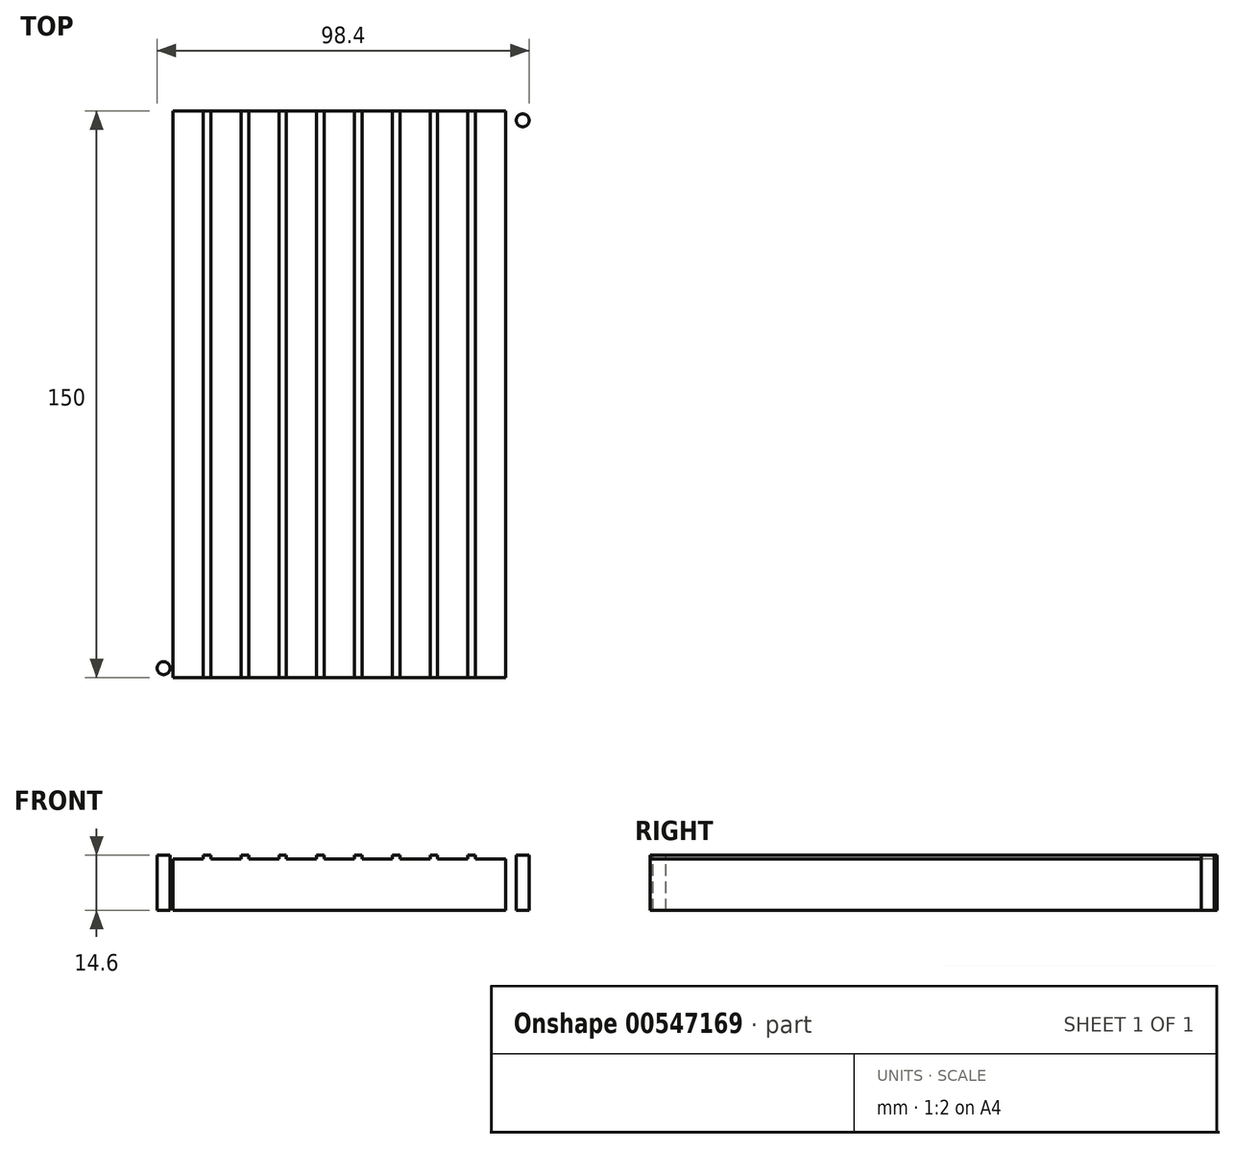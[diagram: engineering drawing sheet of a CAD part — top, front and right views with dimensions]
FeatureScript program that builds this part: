
annotation { "Feature Type Name" : "Feature", "Feature Type Description" : "" }
export const myFeature = defineFeature(function(context is Context, id is Id, definition is map)
    precondition{}
    {
        {
            var Q0;
            Q0=qCreatedBy(makeId("Top.planeOp"),FACE);
            var sketch = newSketch(context, id + "F0", { "sketchPlane" : qUnion([Q0])});
            skLineSegment(sketch, "E0.bottom", {"start": v(0, 0) * mm, "end": v(100, 0) * mm});
            skLineSegment(sketch, "E0.top", {"start": v(0, -150) * mm, "end": v(100, -150) * mm});
            skLineSegment(sketch, "E0.left", {"start": v(0, 0) * mm, "end": v(0, -150) * mm});
            skLineSegment(sketch, "E0.right", {"start": v(100, 0) * mm, "end": v(100, -150) * mm});
            skSolve(sketch);
        }
        {
            var Q0;
            Q0=makeQuery(id+"F0.imprint","IMPRINT",FACE,{"disambiguationData":[TD([[makeQuery(id+"F0.imprint","IMPRINT",EDGE,{"derivedFrom":sQuery(id+"F0.wireOp",EDGE,"E0.bottom")}),-1.0]])]});
            extrude(context, id + "F1", {"entities" : qUnion([Q0]), "depth" : 14.6 * mm, "offsetDistance" : 25 * mm});
        }
        {
            var Q0;
            Q0=makeQuery(id+"F1.opExtrude","CAP_FACE",FACE,{"disambiguationData":[OSD([sQuery(id+"F0.wireOp",EDGE,"E0.bottom"),sQuery(id+"F0.wireOp",EDGE,"E0.top"),sQuery(id+"F0.wireOp",EDGE,"E0.left"),sQuery(id+"F0.wireOp",EDGE,"E0.right")])],"isStart":false});
            var sketch = newSketch(context, id + "F2", { "sketchPlane" : qUnion([Q0])});
            skLineSegment(sketch, "E1.bottom", {"start": v(5, 0) * mm, "end": v(13, 0) * mm});
            skLineSegment(sketch, "E1.top", {"start": v(5, -150) * mm, "end": v(13, -150) * mm});
            skLineSegment(sketch, "E1.left", {"start": v(5, 0) * mm, "end": v(5, -150) * mm});
            skLineSegment(sketch, "E1.right", {"start": v(13, 0) * mm, "end": v(13, -150) * mm});
            skLineSegment(sketch, "E2.1.0.0", {"start": v(15, 0) * mm, "end": v(23, 0) * mm});
            skLineSegment(sketch, "E2.1.0.1", {"start": v(23, 0) * mm, "end": v(23, -150) * mm});
            skLineSegment(sketch, "E2.1.0.2", {"start": v(15, -150) * mm, "end": v(23, -150) * mm});
            skLineSegment(sketch, "E2.1.0.3", {"start": v(15, 0) * mm, "end": v(15, -150) * mm});
            skLineSegment(sketch, "E2.2.0.0", {"start": v(25, 0) * mm, "end": v(33, 0) * mm});
            skLineSegment(sketch, "E2.2.0.1", {"start": v(33, 0) * mm, "end": v(33, -150) * mm});
            skLineSegment(sketch, "E2.2.0.2", {"start": v(25, -150) * mm, "end": v(33, -150) * mm});
            skLineSegment(sketch, "E2.2.0.3", {"start": v(25, 0) * mm, "end": v(25, -150) * mm});
            skLineSegment(sketch, "E2.3.0.0", {"start": v(35, 0) * mm, "end": v(43, 0) * mm});
            skLineSegment(sketch, "E2.3.0.1", {"start": v(43, 0) * mm, "end": v(43, -150) * mm});
            skLineSegment(sketch, "E2.3.0.2", {"start": v(35, -150) * mm, "end": v(43, -150) * mm});
            skLineSegment(sketch, "E2.3.0.3", {"start": v(35, 0) * mm, "end": v(35, -150) * mm});
            skLineSegment(sketch, "E2.4.0.0", {"start": v(45, 0) * mm, "end": v(53, 0) * mm});
            skLineSegment(sketch, "E2.4.0.1", {"start": v(53, 0) * mm, "end": v(53, -150) * mm});
            skLineSegment(sketch, "E2.4.0.2", {"start": v(45, -150) * mm, "end": v(53, -150) * mm});
            skLineSegment(sketch, "E2.4.0.3", {"start": v(45, 0) * mm, "end": v(45, -150) * mm});
            skLineSegment(sketch, "E2.5.0.0", {"start": v(55, 0) * mm, "end": v(63, 0) * mm});
            skLineSegment(sketch, "E2.5.0.1", {"start": v(63, 0) * mm, "end": v(63, -150) * mm});
            skLineSegment(sketch, "E2.5.0.2", {"start": v(55, -150) * mm, "end": v(63, -150) * mm});
            skLineSegment(sketch, "E2.5.0.3", {"start": v(55, 0) * mm, "end": v(55, -150) * mm});
            skLineSegment(sketch, "E2.6.0.0", {"start": v(65, 0) * mm, "end": v(73, 0) * mm});
            skLineSegment(sketch, "E2.6.0.1", {"start": v(73, 0) * mm, "end": v(73, -150) * mm});
            skLineSegment(sketch, "E2.6.0.2", {"start": v(65, -150) * mm, "end": v(73, -150) * mm});
            skLineSegment(sketch, "E2.6.0.3", {"start": v(65, 0) * mm, "end": v(65, -150) * mm});
            skLineSegment(sketch, "E2.7.0.0", {"start": v(75, 0) * mm, "end": v(83, 0) * mm});
            skLineSegment(sketch, "E2.7.0.1", {"start": v(83, 0) * mm, "end": v(83, -150) * mm});
            skLineSegment(sketch, "E2.7.0.2", {"start": v(75, -150) * mm, "end": v(83, -150) * mm});
            skLineSegment(sketch, "E2.7.0.3", {"start": v(75, 0) * mm, "end": v(75, -150) * mm});
            skLineSegment(sketch, "E2.8.0.0", {"start": v(85, 0) * mm, "end": v(93, 0) * mm});
            skLineSegment(sketch, "E2.8.0.1", {"start": v(93, 0) * mm, "end": v(93, -150) * mm});
            skLineSegment(sketch, "E2.8.0.2", {"start": v(85, -150) * mm, "end": v(93, -150) * mm});
            skLineSegment(sketch, "E2.8.0.3", {"start": v(85, 0) * mm, "end": v(85, -150) * mm});
            skLineSegment(sketch, "E2.direction1", {"start": v(5, 0) * mm, "end": v(15, 0) * mm, "construction": true});
            skSolve(sketch);
        }
        {
            var Q0;
            Q0=makeQuery(id+"F2.imprint","IMPRINT",FACE,{"disambiguationData":[TD([[makeQuery(id+"F2.imprint","IMPRINT",EDGE,{"derivedFrom":sQuery(id+"F2.wireOp",EDGE,"E1.bottom")}),-1.0]])]});
            var Q1;
            Q1=makeQuery(id+"F2.imprint","IMPRINT",FACE,{"disambiguationData":[TD([[makeQuery(id+"F2.imprint","IMPRINT",EDGE,{"derivedFrom":sQuery(id+"F2.wireOp",EDGE,"E2.1.0.0")}),-1.0]])]});
            var Q2;
            Q2=makeQuery(id+"F2.imprint","IMPRINT",FACE,{"disambiguationData":[TD([[makeQuery(id+"F2.imprint","IMPRINT",EDGE,{"derivedFrom":sQuery(id+"F2.wireOp",EDGE,"E2.2.0.0")}),-1.0]])]});
            var Q3;
            Q3=makeQuery(id+"F2.imprint","IMPRINT",FACE,{"disambiguationData":[TD([[makeQuery(id+"F2.imprint","IMPRINT",EDGE,{"derivedFrom":sQuery(id+"F2.wireOp",EDGE,"E2.3.0.0")}),-1.0]])]});
            var Q4;
            Q4=makeQuery(id+"F2.imprint","IMPRINT",FACE,{"disambiguationData":[TD([[makeQuery(id+"F2.imprint","IMPRINT",EDGE,{"derivedFrom":sQuery(id+"F2.wireOp",EDGE,"E2.4.0.0")}),-1.0]])]});
            var Q5;
            Q5=makeQuery(id+"F2.imprint","IMPRINT",FACE,{"disambiguationData":[TD([[makeQuery(id+"F2.imprint","IMPRINT",EDGE,{"derivedFrom":sQuery(id+"F2.wireOp",EDGE,"E2.5.0.0")}),-1.0]])]});
            var Q6;
            Q6=makeQuery(id+"F2.imprint","IMPRINT",FACE,{"disambiguationData":[TD([[makeQuery(id+"F2.imprint","IMPRINT",EDGE,{"derivedFrom":sQuery(id+"F2.wireOp",EDGE,"E2.6.0.0")}),-1.0]])]});
            var Q7;
            Q7=makeQuery(id+"F2.imprint","IMPRINT",FACE,{"disambiguationData":[TD([[makeQuery(id+"F2.imprint","IMPRINT",EDGE,{"derivedFrom":sQuery(id+"F2.wireOp",EDGE,"E2.7.0.0")}),-1.0]])]});
            var Q8;
            Q8=makeQuery(id+"F2.imprint","IMPRINT",FACE,{"disambiguationData":[TD([[makeQuery(id+"F2.imprint","IMPRINT",EDGE,{"derivedFrom":sQuery(id+"F2.wireOp",EDGE,"E2.8.0.0")}),-1.0]])]});
            extrude(context, id + "F3", {"entities" : qUnion([Q0, Q1, Q2, Q3, Q4, Q5, Q6, Q7, Q8]), "operationType" : NewBodyOperationType.REMOVE, "oppositeDirection" : true, "depth" : 1 * mm, "offsetDistance" : 25 * mm});
        }
        {
            var Q0;
            {var subQ0=sQuery(id+"F0.wireOp",EDGE,"E0.bottom");var subQ1=sQuery(id+"F0.wireOp",EDGE,"E0.top");var subQ2=sQuery(id+"F0.wireOp",EDGE,"E0.left");Q0=makeQuery(id+"F3.boolean.opBoolean","SPLIT",FACE,{"disambiguationData":[TD([makeQuery(id+"F1.opExtrude","SWEPT_FACE",FACE,{"disambiguationData":[OSD([subQ2])]})])],"derivedFrom":makeQuery(id+"F1.opExtrude","CAP_FACE",FACE,{"disambiguationData":[OSD([subQ0,subQ1,subQ2,sQuery(id+"F0.wireOp",EDGE,"E0.right")])],"isStart":false})});}
            var sketch = newSketch(context, id + "F4", { "sketchPlane" : qUnion([Q0])});
            skCircle(sketch, "E3", {"center": v(2.5, -2.5) * mm, "radius": 1.7 * mm});
            skLineSegment(sketch, "E4", {"start": v(0, -75) * mm, "end": v(-32.3, -75) * mm, "construction": true});
            skLineSegment(sketch, "E5.0.0", {"start": v(100, 0) * mm, "end": v(93, 0) * mm});
            skLineSegment(sketch, "E5.0.1", {"start": v(93, 0) * mm, "end": v(93, -150) * mm});
            skLineSegment(sketch, "E5.0.2", {"start": v(93, -150) * mm, "end": v(100, -150) * mm});
            skLineSegment(sketch, "E5.0.3", {"start": v(100, -150) * mm, "end": v(100, 0) * mm});
            skLineSegment(sketch, "E6.0.0", {"start": v(5, -150) * mm, "end": v(5, 0) * mm});
            skLineSegment(sketch, "E6.0.1", {"start": v(5, 0) * mm, "end": v(0, 0) * mm});
            skLineSegment(sketch, "E6.0.2", {"start": v(0, 0) * mm, "end": v(0, -150) * mm});
            skLineSegment(sketch, "E6.0.3", {"start": v(0, -150) * mm, "end": v(5, -150) * mm});
            skLineSegment(sketch, "E7", {"start": v(0, 0) * mm, "end": v(100, 0) * mm, "construction": true});
            skLineSegment(sketch, "E8", {"start": v(50, 0) * mm, "end": v(50, 30.95) * mm, "construction": true});
            skCircle(sketch, "E9.MirrorC", {"center": v(97.5, -2.5) * mm, "radius": 1.7 * mm});
            skCircle(sketch, "E10.MirrorC", {"center": v(2.5, -147.5) * mm, "radius": 1.7 * mm});
            skCircle(sketch, "E11.MirrorC", {"center": v(97.5, -147.5) * mm, "radius": 1.7 * mm});
            skSolve(sketch);
        }
        {
            var Q0;
            Q0=makeQuery(id+"F4.imprint","IMPRINT",FACE,{"disambiguationData":[TD([[makeQuery(id+"F4.imprint","IMPRINT",EDGE,{"derivedFrom":sQuery(id+"F4.wireOp",EDGE,"E3")}),1.0]])]});
            var Q1;
            Q1=makeQuery(id+"F4.imprint","IMPRINT",FACE,{"disambiguationData":[TD([[makeQuery(id+"F4.imprint","IMPRINT",EDGE,{"derivedFrom":sQuery(id+"F4.wireOp",EDGE,"E10.MirrorC")}),-1.0]])]});
            var Q2;
            Q2=makeQuery(id+"F4.imprint","IMPRINT",FACE,{"disambiguationData":[TD([[makeQuery(id+"F4.imprint","IMPRINT",EDGE,{"derivedFrom":sQuery(id+"F4.wireOp",EDGE,"E11.MirrorC")}),1.0]])]});
            var Q3;
            Q3=makeQuery(id+"F4.imprint","IMPRINT",FACE,{"disambiguationData":[TD([[makeQuery(id+"F4.imprint","IMPRINT",EDGE,{"derivedFrom":sQuery(id+"F4.wireOp",EDGE,"E9.MirrorC")}),-1.0]])]});
            extrude(context, id + "F5", {"entities" : qUnion([Q0, Q1, Q2, Q3]), "operationType" : NewBodyOperationType.REMOVE, "oppositeDirection" : true, "depth" : 25 * mm, "offsetDistance" : 25 * mm});
        }
    });
